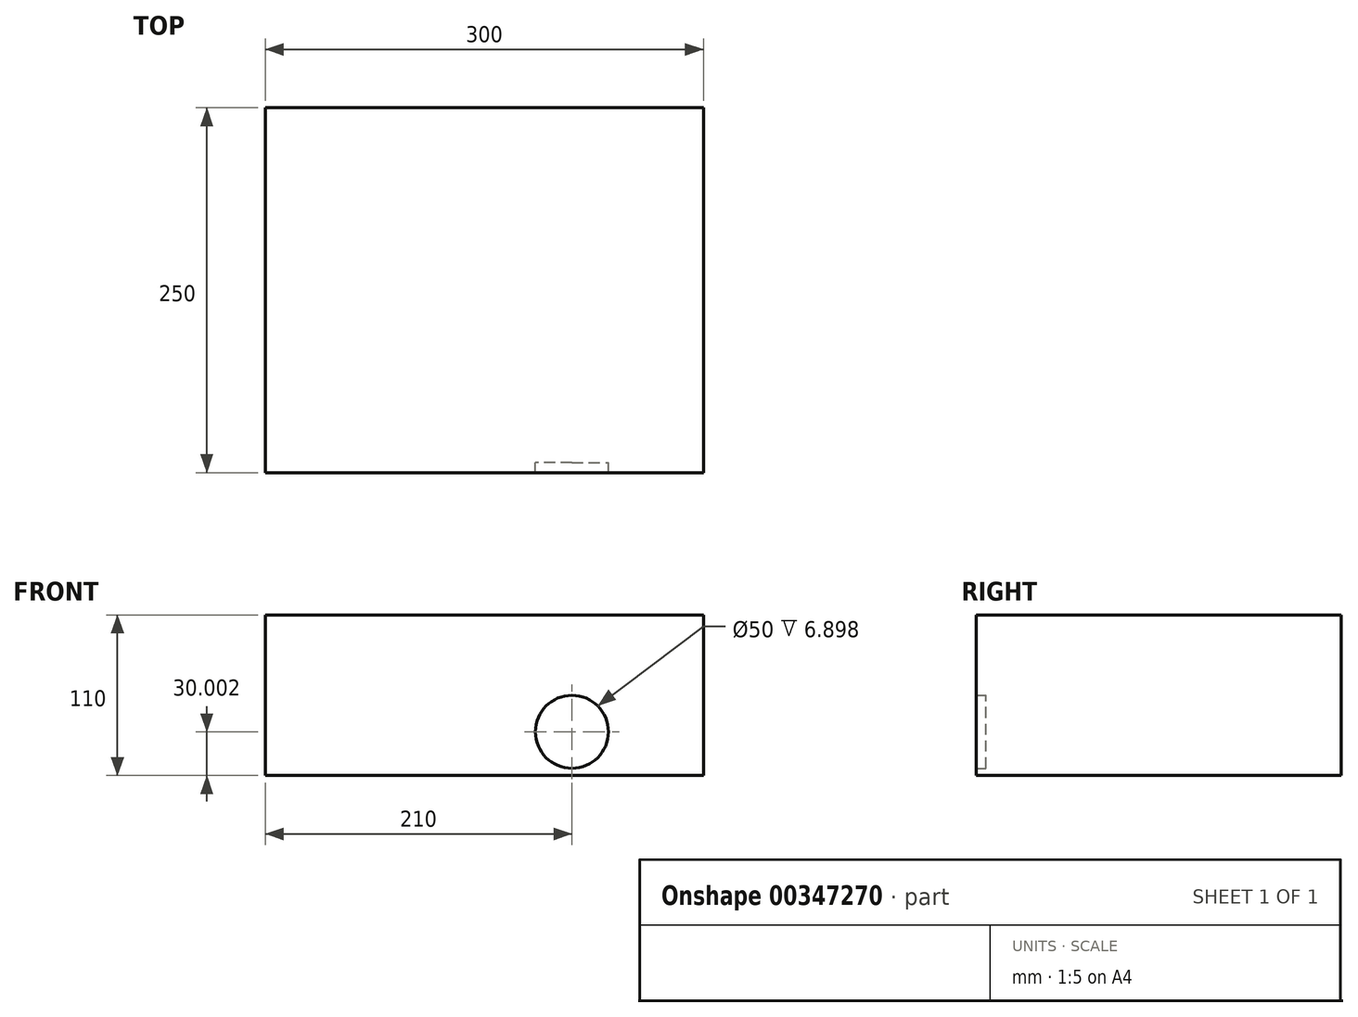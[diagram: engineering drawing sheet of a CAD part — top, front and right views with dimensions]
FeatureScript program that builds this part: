
annotation { "Feature Type Name" : "Feature", "Feature Type Description" : "" }
export const myFeature = defineFeature(function(context is Context, id is Id, definition is map)
    precondition{}
    {
        {
            var Q0;
            Q0=qCreatedBy(makeId("Right.planeOp"),FACE);
            var sketch = newSketch(context, id + "F0", { "sketchPlane" : qUnion([Q0])});
            skLineSegment(sketch, "E0.bottom", {"start": v(-128.9, 109.97) * mm, "end": v(121.1, 109.97) * mm});
            skLineSegment(sketch, "E0.top", {"start": v(-128.9, -0.03) * mm, "end": v(121.1, -0.03) * mm});
            skLineSegment(sketch, "E0.left", {"start": v(-128.9, 109.97) * mm, "end": v(-128.9, -0.03) * mm});
            skLineSegment(sketch, "E0.right", {"start": v(121.1, 109.97) * mm, "end": v(121.1, -0.03) * mm});
            skSolve(sketch);
        }
        {
            var Q0;
            Q0 = qSketchRegion(id + "F0", true);
            extrude(context, id + "F1", {"entities" : qUnion([Q0]), "depth" : 300 * mm, "symmetric" : true});
        }
        {
            var Q0;
            Q0=qCreatedBy(makeId("Front.planeOp"),FACE);
            var sketch = newSketch(context, id + "F2", { "sketchPlane" : qUnion([Q0])});
            skCircle(sketch, "E1", {"center": v(60, 29.97) * mm, "radius": 25 * mm});
            skSolve(sketch);
        }
        {
            var Q0;
            Q0 = qSketchRegion(id + "F2", true);
            extrude(context, id + "F3", {"entities" : qUnion([Q0]), "operationType" : NewBodyOperationType.REMOVE, "depth" : 202 * mm, "hasSecondDirection" : true, "secondDirectionOppositeDirection" : false, "secondDirectionDepth" : 122 * mm});
        }
    });
